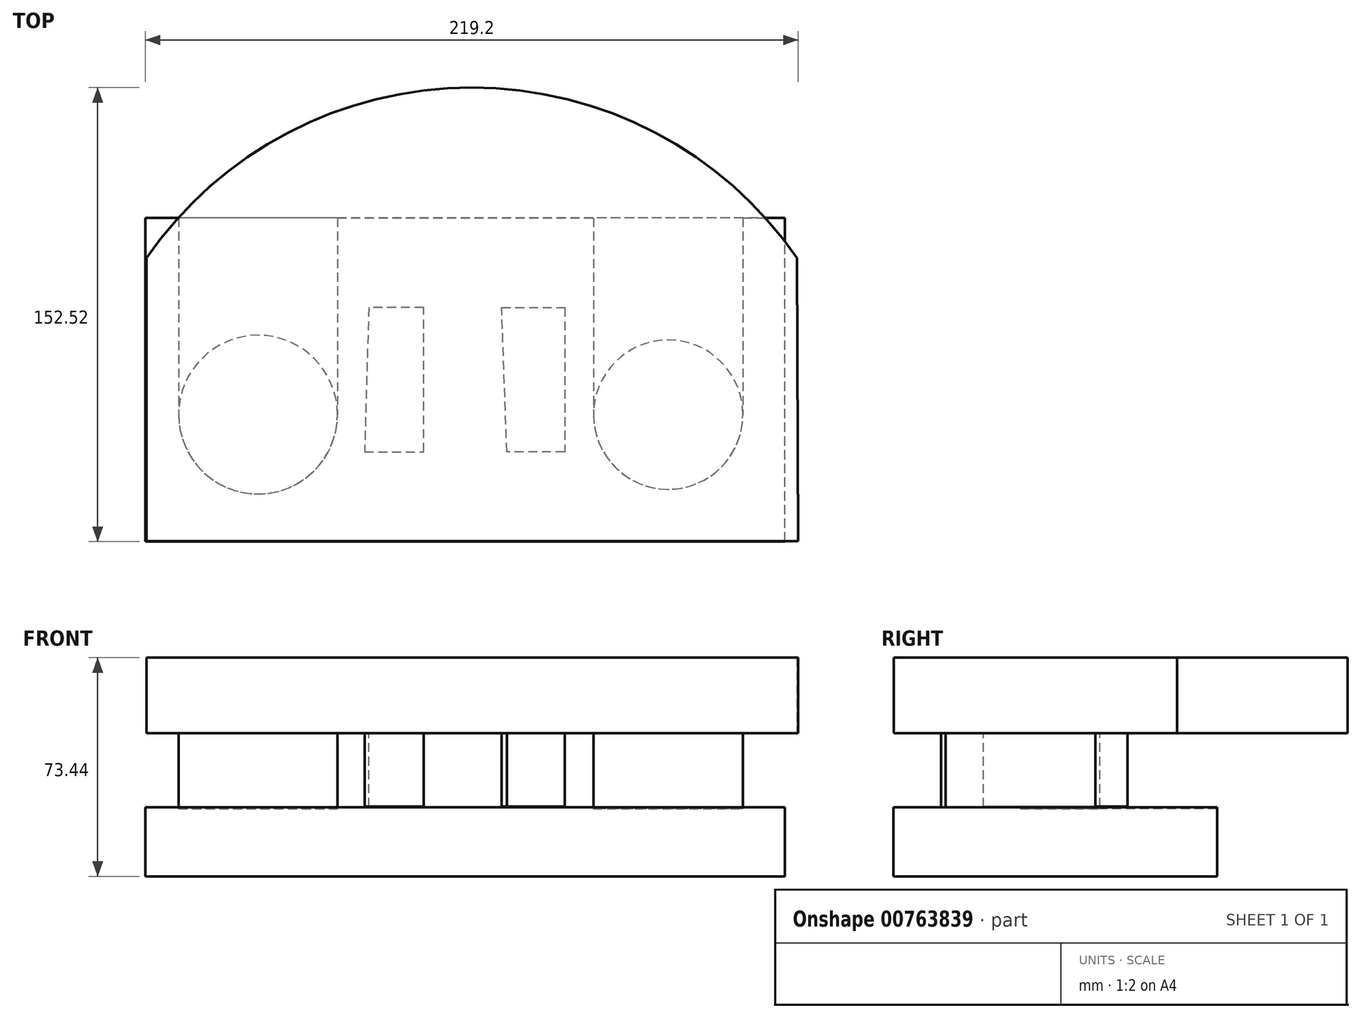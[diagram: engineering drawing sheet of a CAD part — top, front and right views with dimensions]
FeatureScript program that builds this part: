
annotation { "Feature Type Name" : "Feature", "Feature Type Description" : "" }
export const myFeature = defineFeature(function(context is Context, id is Id, definition is map)
    precondition{}
    {
        {
            var Q0;
            Q0=qCreatedBy(makeId("Top.planeOp"),FACE);
            var sketch = newSketch(context, id + "F0", { "sketchPlane" : qUnion([Q0])});
            skLineSegment(sketch, "E0", {"start": v(114.4, -42.5) * mm, "end": v(-64.76, -42.5) * mm});
            skLineSegment(sketch, "E1", {"start": v(-64.76, -42.5) * mm, "end": v(-104.45, -42.5) * mm});
            skLineSegment(sketch, "E2", {"start": v(-104.45, -42.5) * mm, "end": v(-104.45, 43.54) * mm});
            skLineSegment(sketch, "E3", {"start": v(-104.45, 43.54) * mm, "end": v(-104.45, 52.62) * mm});
            skLineSegment(sketch, "E4", {"start": v(-104.45, 52.62) * mm, "end": v(114.07, 52.62) * mm});
            skLineSegment(sketch, "E5", {"start": v(114.07, 52.62) * mm, "end": v(114.4, -42.5) * mm});
            skArc(sketch, "E6", {"start": v(114.07, 52.62) * mm, "mid": v(4.8, 109.85) * mm, "end": v(-104.45, 52.62) * mm});
            skSolve(sketch);
        }
        {
            var Q0;
            Q0=makeQuery(id+"F0.imprint","IMPRINT",FACE,{"disambiguationData":[TD([[makeQuery(id+"F0.imprint","IMPRINT",EDGE,{"derivedFrom":sQuery(id+"F0.wireOp",EDGE,"E0")}),-1.0]])]});
            var Q1;
            Q1=makeQuery(id+"F0.imprint","IMPRINT",FACE,{"disambiguationData":[TD([[makeQuery(id+"F0.imprint","IMPRINT",EDGE,{"derivedFrom":sQuery(id+"F0.wireOp",EDGE,"E4")}),1.0]])]});
            extrude(context, id + "F1", {"entities" : qUnion([Q0, Q1]), "depth" : 25.4 * mm, "offsetDistance" : 25.4 * mm});
        }
        {
            var Q0;
            Q0=makeQuery(id+"F1.opExtrude","CAP_FACE",FACE,{"disambiguationData":[OSD([sQuery(id+"F0.wireOp",EDGE,"E0"),sQuery(id+"F0.wireOp",EDGE,"E1"),sQuery(id+"F0.wireOp",EDGE,"E2"),sQuery(id+"F0.wireOp",EDGE,"E3"),sQuery(id+"F0.wireOp",EDGE,"E5"),sQuery(id+"F0.wireOp",EDGE,"E6")])],"isStart":true});
            var sketch = newSketch(context, id + "F2", { "sketchPlane" : qUnion([Q0])});
            skCircle(sketch, "E7", {"center": v(70.77, 0) * mm, "radius": 25.1 * mm});
            skCircle(sketch, "E8", {"center": v(-66.95, 0) * mm, "radius": 26.66 * mm});
            skSolve(sketch);
        }
        {
            var Q0;
            Q0=makeQuery(id+"F1.opExtrude","CAP_FACE",FACE,{"disambiguationData":[OSD([sQuery(id+"F0.wireOp",EDGE,"E0"),sQuery(id+"F0.wireOp",EDGE,"E1"),sQuery(id+"F0.wireOp",EDGE,"E2"),sQuery(id+"F0.wireOp",EDGE,"E3"),sQuery(id+"F0.wireOp",EDGE,"E5"),sQuery(id+"F0.wireOp",EDGE,"E6")])],"isStart":false});
            var sketch = newSketch(context, id + "F3", { "sketchPlane" : qUnion([Q0])});
            skLineSegment(sketch, "E9", {"start": v(-31.15, -12.5) * mm, "end": v(-11.38, -12.5) * mm});
            skLineSegment(sketch, "E10", {"start": v(-11.38, -12.5) * mm, "end": v(-11.38, 35.91) * mm});
            skLineSegment(sketch, "E11", {"start": v(-11.38, 35.91) * mm, "end": v(-29.8, 35.91) * mm});
            skLineSegment(sketch, "E12", {"start": v(-29.8, 35.91) * mm, "end": v(-31.15, -12.5) * mm});
            skLineSegment(sketch, "E13", {"start": v(14.87, 35.91) * mm, "end": v(36, 35.91) * mm});
            skLineSegment(sketch, "E14", {"start": v(36, 35.91) * mm, "end": v(36, -12.5) * mm});
            skLineSegment(sketch, "E15", {"start": v(36, -12.5) * mm, "end": v(16.57, -12.5) * mm});
            skLineSegment(sketch, "E16", {"start": v(16.57, -12.5) * mm, "end": v(14.87, 35.91) * mm});
            skSolve(sketch);
        }
        {
            var Q0;
            Q0=makeQuery(id+"F3.imprint","IMPRINT",FACE,{"disambiguationData":[TD([[makeQuery(id+"F3.imprint","IMPRINT",EDGE,{"derivedFrom":sQuery(id+"F3.wireOp",EDGE,"E9")}),1.0]])]});
            var Q1;
            Q1=makeQuery(id+"F3.imprint","IMPRINT",FACE,{"disambiguationData":[TD([[makeQuery(id+"F3.imprint","IMPRINT",EDGE,{"derivedFrom":sQuery(id+"F3.wireOp",EDGE,"E13")}),-1.0]])]});
            extrude(context, id + "F4", {"entities" : qUnion([Q0, Q1]), "operationType" : NewBodyOperationType.ADD, "oppositeDirection" : true, "depth" : 50.04 * mm, "offsetDistance" : 25.4 * mm});
        }
        {
            var Q0;
            Q0=makeQuery(id+"F2.imprint","IMPRINT",FACE,{"disambiguationData":[TD([[makeQuery(id+"F2.imprint","IMPRINT",EDGE,{"derivedFrom":sQuery(id+"F2.wireOp",EDGE,"E7")}),1.0]])]});
            var Q1;
            Q1=makeQuery(id+"F2.imprint","IMPRINT",FACE,{"disambiguationData":[TD([[makeQuery(id+"F2.imprint","IMPRINT",EDGE,{"derivedFrom":sQuery(id+"F2.wireOp",EDGE,"E8")}),1.0]])]});
            extrude(context, id + "F5", {"entities" : qUnion([Q0, Q1]), "operationType" : NewBodyOperationType.ADD, "depth" : 25.4 * mm, "offsetDistance" : 25.4 * mm});
        }
        {
            var Q0;
            Q0=qCreatedBy(makeId("Front.planeOp"),FACE);
            var sketch = newSketch(context, id + "F6", { "sketchPlane" : qUnion([Q0])});
            skLineSegment(sketch, "E17", {"start": v(-104.79, -44.66) * mm, "end": v(-104.79, -29.32) * mm});
            skLineSegment(sketch, "E18", {"start": v(-104.79, -29.32) * mm, "end": v(-104.79, -24.89) * mm});
            skLineSegment(sketch, "E19", {"start": v(-104.79, -24.89) * mm, "end": v(109.98, -24.89) * mm});
            skLineSegment(sketch, "E20", {"start": v(109.98, -24.89) * mm, "end": v(109.98, -48.04) * mm});
            skLineSegment(sketch, "E21", {"start": v(109.98, -48.04) * mm, "end": v(-104.79, -48.04) * mm});
            skLineSegment(sketch, "E22", {"start": v(-104.79, -48.04) * mm, "end": v(-104.79, -24.89) * mm});
            skSolve(sketch);
        }
        {
            var Q0;
            {var subQ0=sQuery(id+"F6.wireOp",EDGE,"E19");Q0=makeQuery(id+"F6.imprint","IMPRINT",FACE,{"disambiguationData":[TD([[makeQuery(id+"F6.imprint","IMPRINT",EDGE,{"derivedFrom":subQ0}),-1.0]])]});}
            extrude(context, id + "F7", {"entities" : qUnion([Q0]), "operationType" : NewBodyOperationType.ADD, "depth" : 42.67 * mm, "offsetDistance" : 25.4 * mm});
        }
        {
            var Q0;
            Q0=makeQuery(id+"F7.opExtrude","CAP_FACE",FACE,{"disambiguationData":[OSD([sQuery(id+"F6.wireOp",EDGE,"E19"),sQuery(id+"F6.wireOp",EDGE,"E20"),sQuery(id+"F6.wireOp",EDGE,"E21"),sQuery(id+"F6.wireOp",EDGE,"E22")])],"isStart":true});
            extrude(context, id + "F8", {"entities" : qUnion([Q0]), "operationType" : NewBodyOperationType.ADD, "depth" : 38.1 * mm, "offsetDistance" : 25.4 * mm});
        }
        {
            var Q0;
            Q0=makeQuery(id+"F8.opExtrude","CAP_FACE",FACE,{"disambiguationData":[OSD([sQuery(id+"F6.wireOp",EDGE,"E19"),sQuery(id+"F6.wireOp",EDGE,"E20"),sQuery(id+"F6.wireOp",EDGE,"E21"),sQuery(id+"F6.wireOp",EDGE,"E22")])],"isStart":false});
            extrude(context, id + "F9", {"entities" : qUnion([Q0]), "operationType" : NewBodyOperationType.ADD, "depth" : 27.94 * mm, "offsetDistance" : 25.4 * mm});
        }
    });
